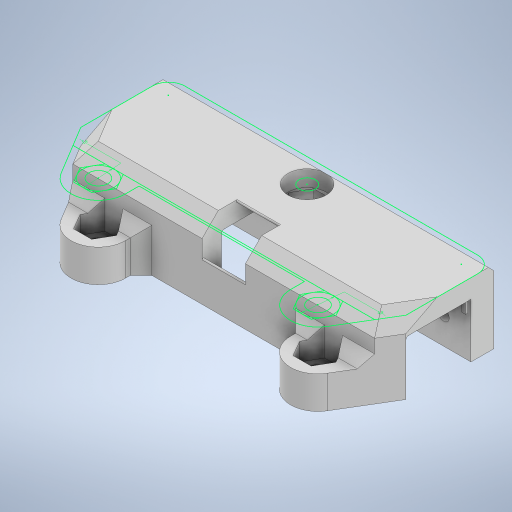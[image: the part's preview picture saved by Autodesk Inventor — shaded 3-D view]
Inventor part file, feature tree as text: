
AUTODESK INVENTOR PART (.ipt)
format: ipt  version: 2023 (Build 270158000, 158)  size: 585,216 bytes
history: native  units: mm
features: extrude x15, sketch x14, projected_geometry x12, chamfer x4, fillet x4, other x1, hole x1
ambient origin geometry x8: Origin, YZ Plane, XZ Plane, XY Plane, X Axis, Y Axis, Z Axis, Center Point
bodies: Body1 (feature_tree)
feature tree (51):
  other  "Bryła1"
  extrude  "Wyciągnięcie proste1"  Depth=10.0mm
  extrude  "Wyciągnięcie proste2"  Depth=10.0mm
  extrude  "Wyciągnięcie proste3"  Depth=10.0mm
  sketch  "Szkic4"
  extrude  "Wyciągnięcie proste4"  Depth=10.0mm TaperAngle=0.0deg
  extrude  "Wyciągnięcie proste5"  Depth=3.5mm TaperAngle=0.0deg
  extrude  "Wyciągnięcie proste6"  Depth=4.0mm
  sketch  "Szkic6"
  extrude  "Wyciągnięcie proste7"  Depth=3.5mm TaperAngle=0.0deg
  extrude  "Wyciągnięcie proste8"  Depth=5.8mm
  extrude  "Wyciągnięcie proste9"  Depth=5.8mm
  extrude  "Wyciągnięcie proste10"  Depth=7.5mm TaperAngle=0.0deg
  extrude  "Wyciągnięcie proste12"  Depth=10.8mm TaperAngle=0.0deg
  chamfer  "Faza1"  [1 undecoded]
  fillet  "Zaokrąglenie3"  Radius=5.8mm
  fillet  "Zaokrąglenie4"  Radius=7.0mm
  chamfer  "Faza2"  Distance=3.0mm
  chamfer  "Faza3"  Distance=6.0mm
  extrude  "Wyciągnięcie proste13"  Depth=0.7mm
  extrude  "Wyciągnięcie proste14"  Depth=3.0mm
  chamfer  "Faza4"  Distance=0.6mm
  extrude  "Wyciągnięcie proste15"  Depth=2.0mm
  extrude  "Wyciągnięcie proste16"  Depth=5.1mm
  fillet  "Zaokrąglenie6"  Radius=3.0mm
  fillet  "Zaokrąglenie7"  Radius=0.4mm
  hole  "Otwór1"  [1 undecoded]
  sketch  "Szkic1"
  sketch  "Szkic2"
  projected_geometry  "Pętla rzutowana1"
  projected_geometry  "Pętla rzutowana2"
  projected_geometry  "Pętla rzutowana3"
  sketch  "Szkic3"
  projected_geometry  "Pętla rzutowana4"
  projected_geometry  "Pętla rzutowana5"
  projected_geometry  "Pętla rzutowana6"
  sketch  "Szkic5"
  projected_geometry  "Pętla rzutowana7"
  sketch  "Szkic7"
  projected_geometry  "Pętla rzutowana8"
  sketch  "Szkic8"
  sketch  "Szkic10"
  sketch  "Szkic11"
  projected_geometry  "Pętla rzutowana9"
  sketch  "Szkic12"
  projected_geometry  "Pętla rzutowana10"
  sketch  "Szkic13"
  sketch  "Szkic14"
  projected_geometry  "Pętla rzutowana11"
  sketch  "Szkic15"
  projected_geometry  "Pętla rzutowana12"
note: 2 required parameter values undecoded (feature->parameter linkage not recoverable at this tier; creation-order binding heuristic only, values carry confidence <= 0.55)
